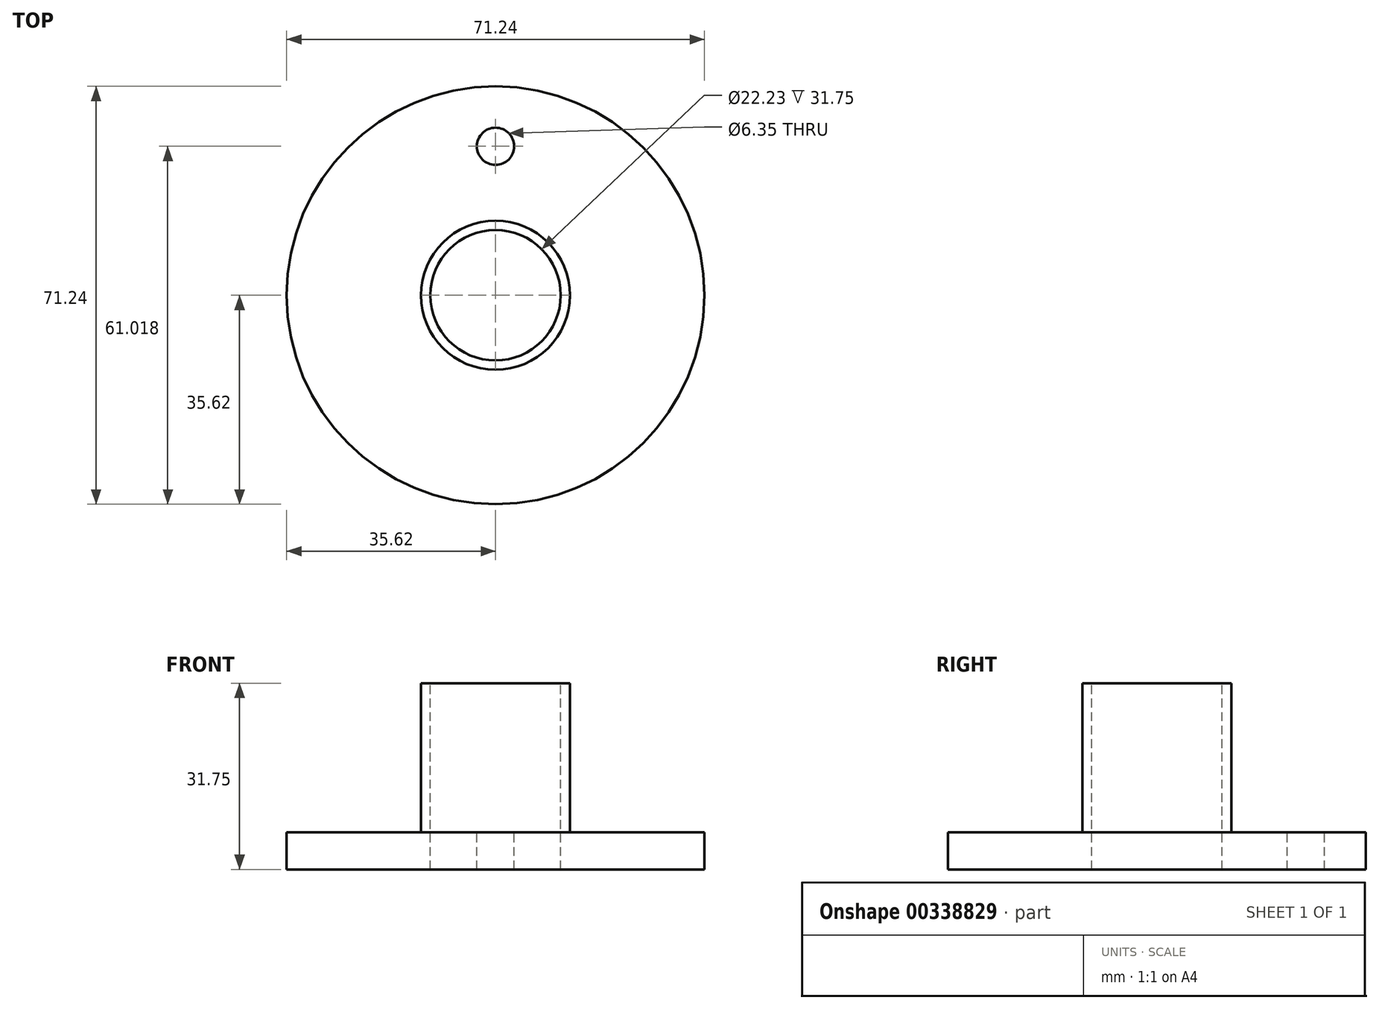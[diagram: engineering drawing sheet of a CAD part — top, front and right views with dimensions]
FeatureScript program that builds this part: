
annotation { "Feature Type Name" : "Feature", "Feature Type Description" : "" }
export const myFeature = defineFeature(function(context is Context, id is Id, definition is map)
    precondition{}
    {
        {
            var Q0;
            Q0=qCreatedBy(makeId("Front.planeOp"),FACE);
            var sketch = newSketch(context, id + "F0", { "sketchPlane" : qUnion([Q0])});
            skLineSegment(sketch, "E0", {"start": v(0, 0) * mm, "end": v(35.62, 0) * mm});
            skLineSegment(sketch, "E1", {"start": v(35.62, 0) * mm, "end": v(35.62, 6.35) * mm});
            skLineSegment(sketch, "E2", {"start": v(35.62, 6.35) * mm, "end": v(12.7, 6.35) * mm});
            skLineSegment(sketch, "E3", {"start": v(12.7, 6.35) * mm, "end": v(12.7, 31.75) * mm});
            skLineSegment(sketch, "E4", {"start": v(12.7, 31.75) * mm, "end": v(0, 31.75) * mm});
            skLineSegment(sketch, "E5", {"start": v(0, 31.75) * mm, "end": v(0, 0) * mm});
            skSolve(sketch);
        }
        {
            var Q0;
            Q0 = qSketchRegion(id + "F0", true);
            var Q1;
            Q1=sQuery(id+"F0.wireOp",EDGE,"E5");
            revolve(context, id + "F1", {"entities" : qUnion([Q0]), "axis" : qUnion([Q1]), "revolveType" : RevolveType.FULL});
        }
        {
            var Q0;
            Q0=makeQuery(id+"F1.opRevolve","SWEPT_FACE",FACE,{"disambiguationData":[OSD([sQuery(id+"F0.wireOp",EDGE,"E4")])]});
            var sketch = newSketch(context, id + "F2", { "sketchPlane" : qUnion([Q0])});
            skPoint(sketch, "E6", {"position": v(0, 0) * mm});
            skSolve(sketch);
        }
        {
            var Q0;
            Q0=sQuery(id+"F2.wireOp",VERTEX,"E6");
            var Q1;
            Q1=makeQuery(id+"F1.opRevolve","SWEPT_BODY",BODY,{"disambiguationData":[OSD([sQuery(id+"F0.wireOp",EDGE,"E0"),sQuery(id+"F0.wireOp",EDGE,"E1"),sQuery(id+"F0.wireOp",EDGE,"E2"),sQuery(id+"F0.wireOp",EDGE,"E3"),sQuery(id+"F0.wireOp",EDGE,"E4"),sQuery(id+"F0.wireOp",EDGE,"E5")])]});
            hole(context, id + "F3", {"style" : HoleStyle.SIMPLE, "endStyle" : HoleEndStyle.THROUGH, "holeDiameter" : 22.22 * mm, "isTappedThrough" : true, "tappedDepth" : 12.7 * mm, "tapClearance" : 3, "locations" : qUnion([Q0]), "scope" : qUnion([Q1])});
        }
        {
            var Q0;
            Q0=makeQuery(id+"F1.opRevolve","SWEPT_FACE",FACE,{"disambiguationData":[OSD([sQuery(id+"F0.wireOp",EDGE,"E2")])]});
            var sketch = newSketch(context, id + "F4", { "sketchPlane" : qUnion([Q0])});
            skLineSegment(sketch, "E7", {"start": v(0, 0) * mm, "end": v(0, 25.4) * mm});
            skSolve(sketch);
        }
        {
            var Q0;
            Q0=sQuery(id+"F4.wireOp",VERTEX,"E7.end");
            var Q1;
            Q1=makeQuery(id+"F1.opRevolve","SWEPT_BODY",BODY,{"disambiguationData":[OSD([sQuery(id+"F0.wireOp",EDGE,"E0"),sQuery(id+"F0.wireOp",EDGE,"E1"),sQuery(id+"F0.wireOp",EDGE,"E2"),sQuery(id+"F0.wireOp",EDGE,"E3"),sQuery(id+"F0.wireOp",EDGE,"E4"),sQuery(id+"F0.wireOp",EDGE,"E5")])]});
            hole(context, id + "F5", {"style" : HoleStyle.SIMPLE, "endStyle" : HoleEndStyle.THROUGH, "holeDiameter" : 6.35 * mm, "isTappedThrough" : true, "tappedDepth" : 12.7 * mm, "tapClearance" : 3, "locations" : qUnion([Q0]), "scope" : qUnion([Q1])});
        }
    });
